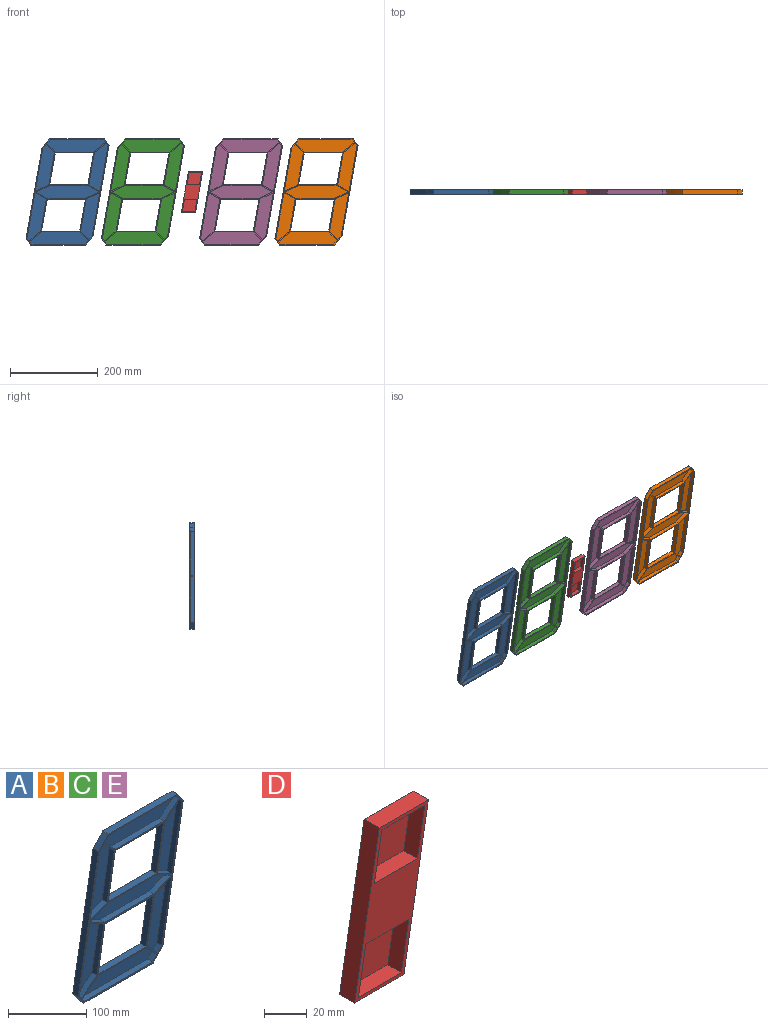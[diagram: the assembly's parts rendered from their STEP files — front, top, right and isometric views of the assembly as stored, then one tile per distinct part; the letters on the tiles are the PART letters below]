
ASSEMBLY  parts=5 mates=4
PART A: 63 faces, bbox 189.5x10x242 mm
  f0: plane 242x189.52mm, normal (0,-1,0), area 3330.4mm2, adj f2,f3,f4,f5,f7,f8,f9,f10
  f1: plane 242x189.52mm, normal (0,1,0), area 23631.7mm2, adj f47,f48,f49,f50,f51,f52,f53,f54
  f2: plane 73.98x13.05mm, normal (-0.98,0,0.17), area 676.1mm2, adj f0,f3,f4,f6
  f3: plane 19.82x18.86mm, normal (-0.72,0,-0.69), area 246.2mm2, adj f0,f2,f5,f6
  f4: plane 30.9x14mm, normal (-0.41,0,0.91), area 305.3mm2, adj f0,f2,f6,f7
  f5: plane 9x8.06mm, normal (0.73,0,-0.68), area 99.1mm2, adj f0,f3,f6,f7
  f6: plane 107.8x43.95mm, normal (0,-1,0), area 2620mm2, adj f2,f3,f4,f5,f7
  f7: plane 99.74x17.59mm, normal (0.98,0,-0.17), area 911.5mm2, adj f0,f4,f5,f6
  f8: plane 31.07x14.08mm, normal (-0.41,0,0.91), area 307mm2, adj f0,f10,f12,f13
  f9: plane 88.61x9mm, normal (0,0,-1), area 797.5mm2, adj f0,f12,f13,f14
  f10: plane 88.61x9mm, normal (0,0,1), area 797.5mm2, adj f0,f8,f11,f13
  f11: plane 25.82x13.92mm, normal (0.47,0,0.88), area 264mm2, adj f0,f10,f13,f14
  f12: plane 25.82x13.92mm, normal (-0.47,0,-0.88), area 264mm2, adj f0,f8,f9,f13
  f13: plane 145.5x28mm, normal (0,-1,0), area 3277mm2, adj f8,f9,f10,f11,f12,f14
  f14: plane 31.07x14.08mm, normal (0.41,0,-0.91), area 307mm2, adj f0,f9,f11,f13
  f15: plane 9x5.74mm, normal (0.82,0,0.57), area 63.1mm2, adj f0,f16,f17,f18
  f16: plane 110.05x44.36mm, normal (0,-1,0), area 2656.6mm2, adj f15,f17,f18,f19,f20
  f17: plane 104.31x18.39mm, normal (0.98,0,-0.17), area 953.3mm2, adj f0,f15,f16,f20
  f18: plane 27.3x22.13mm, normal (-0.63,0,0.78), area 316.3mm2, adj f0,f15,f16,f19
  f19: plane 73.92x13.03mm, normal (-0.98,0,0.17), area 675.6mm2, adj f0,f16,f18,f20
  f20: plane 25.96x14mm, normal (-0.47,0,-0.88), area 265.5mm2, adj f0,f16,f17,f19
  f21: plane 104.31x18.39mm, normal (-0.98,0,0.17), area 953.3mm2, adj f0,f22,f23,f25
  f22: plane 9x5.74mm, normal (-0.82,0,-0.57), area 63.1mm2, adj f0,f21,f23,f24
  f23: plane 110.05x44.36mm, normal (0,-1,0), area 2656.6mm2, adj f21,f22,f24,f25,f26
  f24: plane 27.3x22.13mm, normal (0.63,0,-0.78), area 316.3mm2, adj f0,f22,f23,f26
  f25: plane 25.96x14mm, normal (0.47,0,0.88), area 265.5mm2, adj f0,f21,f23,f26
  f26: plane 73.92x13.03mm, normal (0.98,0,-0.17), area 675.6mm2, adj f0,f23,f24,f25
  f27: plane 9x8.04mm, normal (-0.73,0,0.68), area 98.9mm2, adj f0,f28,f29,f33
  f28: plane 134.7x28mm, normal (0,-1,0), area 3235.6mm2, adj f27,f29,f30,f31,f32,f33
  f29: plane 123.17x9mm, normal (0,0,1), area 1108.5mm2, adj f0,f27,f28,f30
  f30: plane 9x5.77mm, normal (0.82,0,0.57), area 63.4mm2, adj f0,f28,f29,f32
  f31: plane 88.29x9mm, normal (0,0,-1), area 794.6mm2, adj f0,f28,f32,f33
  f32: plane 27.42x22.23mm, normal (0.63,0,-0.78), area 317.7mm2, adj f0,f28,f30,f31
  f33: plane 19.96x18.99mm, normal (-0.72,0,-0.69), area 247.9mm2, adj f0,f27,f28,f31
  f34: plane 27.42x22.23mm, normal (-0.63,0,0.78), area 317.7mm2, adj f0,f36,f37,f38
  f35: plane 123.17x9mm, normal (0,0,-1), area 1108.5mm2, adj f0,f36,f38,f40
  f36: plane 9x5.77mm, normal (-0.82,0,-0.57), area 63.4mm2, adj f0,f34,f35,f38
  f37: plane 88.29x9mm, normal (0,0,1), area 794.6mm2, adj f0,f34,f38,f39
  f38: plane 134.7x28mm, normal (0,-1,0), area 3235.6mm2, adj f34,f35,f36,f37,f39,f40
  f39: plane 19.96x18.99mm, normal (0.72,0,0.69), area 247.9mm2, adj f0,f37,f38,f40
  f40: plane 9x8.04mm, normal (0.73,0,-0.68), area 98.9mm2, adj f0,f35,f38,f39
  f41: plane 99.74x17.59mm, normal (-0.98,0,0.17), area 911.5mm2, adj f0,f42,f43,f44
  f42: plane 9x8.06mm, normal (-0.73,0,0.68), area 99.1mm2, adj f0,f41,f44,f45
  f43: plane 30.9x14mm, normal (0.41,0,-0.91), area 305.3mm2, adj f0,f41,f44,f46
  f44: plane 107.8x43.95mm, normal (0,-1,0), area 2620mm2, adj f41,f42,f43,f45,f46
  f45: plane 19.82x18.86mm, normal (0.72,0,0.69), area 246.2mm2, adj f0,f42,f44,f46
  f46: plane 73.98x13.05mm, normal (0.98,0,-0.17), area 676.1mm2, adj f0,f43,f44,f45
  f47: plane 18.63x17.36mm, normal (-0.73,0,0.68), area 254.6mm2, adj f0,f1,f48,f49
  f48: plane 208.68x36.8mm, normal (-0.98,0,0.17), area 2119mm2, adj f0,f1,f47,f50
  f49: plane 125.08x10mm, normal (0,0,1), area 1250.8mm2, adj f0,f1,f47,f54
  f50: plane 14.68x10.3mm, normal (-0.82,0,-0.57), area 179.3mm2, adj f0,f1,f48,f51
  f51: plane 125.08x10mm, normal (0,0,-1), area 1250.8mm2, adj f0,f1,f50,f52
  f52: plane 18.63x17.36mm, normal (0.73,0,-0.68), area 254.6mm2, adj f0,f1,f51,f53
  f53: plane 208.68x36.8mm, normal (0.98,0,-0.17), area 2119mm2, adj f0,f1,f52,f54
  f54: plane 14.68x10.3mm, normal (0.82,0,0.57), area 179.3mm2, adj f0,f1,f49,f53
  f55: plane 87.04x10mm, normal (0,0,1), area 870.4mm2, adj f0,f1,f56,f57
  f56: plane 73x12.87mm, normal (-0.98,0,0.17), area 741.3mm2, adj f0,f1,f55,f58
  f57: plane 73x12.87mm, normal (0.98,0,-0.17), area 741.3mm2, adj f0,f1,f55,f58
  f58: plane 87.04x10mm, normal (0,0,-1), area 870.4mm2, adj f0,f1,f56,f57
  f59: plane 87.04x10mm, normal (0,0,-1), area 870.4mm2, adj f0,f1,f60,f61
  f60: plane 73x12.87mm, normal (0.98,0,-0.17), area 741.3mm2, adj f0,f1,f59,f62
  f61: plane 73x12.87mm, normal (-0.98,0,0.17), area 741.3mm2, adj f0,f1,f59,f62
  f62: plane 87.04x10mm, normal (0,0,1), area 870.4mm2, adj f0,f1,f60,f61
PART B: same geometry as A
PART C: same geometry as A
PART D: 16 faces, bbox 48.7x10x92 mm
  f0: plane 92x48.72mm, normal (0,-1,0), area 1397.2mm2, adj f1,f2,f3,f4,f6,f7,f8,f9
  f1: plane 28x9mm, normal (-0.98,0,0.17), area 255.9mm2, adj f0,f2,f4,f5
  f2: plane 28.43x9mm, normal (0,0,-1), area 255.9mm2, adj f0,f1,f3,f5
  f3: plane 28x9mm, normal (0.98,0,-0.17), area 255.9mm2, adj f0,f2,f4,f5
  f4: plane 28.43x9mm, normal (0,0,1), area 255.9mm2, adj f0,f1,f3,f5
  f5: plane 33.37x28mm, normal (0,-1,0), area 796.1mm2, adj f1,f2,f3,f4
  f6: plane 28x9mm, normal (-0.98,0,0.17), area 255.9mm2, adj f0,f7,f9,f10
  f7: plane 28.43x9mm, normal (0,0,-1), area 255.9mm2, adj f0,f6,f8,f10
  f8: plane 28x9mm, normal (0.98,0,-0.17), area 255.9mm2, adj f0,f7,f9,f10
  f9: plane 28.43x9mm, normal (0,0,1), area 255.9mm2, adj f0,f6,f8,f10
  f10: plane 33.37x28mm, normal (0,-1,0), area 796.1mm2, adj f6,f7,f8,f9
  f11: plane 92x16.22mm, normal (0.98,0,-0.17), area 934.2mm2, adj f0,f12,f13,f15
  f12: plane 32.49x10mm, normal (0,0,-1), area 324.9mm2, adj f0,f11,f14,f15
  f13: plane 32.49x10mm, normal (0,0,1), area 324.9mm2, adj f0,f11,f14,f15
  f14: plane 92x16.22mm, normal (-0.98,0,0.17), area 934.2mm2, adj f0,f12,f13,f15
  f15: plane 92x48.72mm, normal (0,1,0), area 2989.4mm2, adj f11,f12,f13,f14
PART E: same geometry as A
PLACE A at identity fixed
PLACE B t=(568,0,0)mm
PLACE C t=(172,0,0)mm
PLACE D t=(196.84,0,75)mm
PLACE E t=(396,0,0)mm
MATE fastened C.f1 <-> D.f15  axis (0,1,0) through (118.16,0,120)mm
MATE fastened B.f1 <-> E.f1  axis (0,1,0) through (514.16,0,120)mm
MATE fastened E.f1 <-> D.f15  axis (0,1,0) through (342.16,0,120)mm
MATE fastened C.f1 <-> A.f1  axis (0,1,0) through (118.16,0,120)mm
